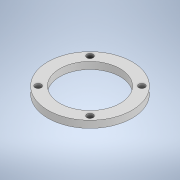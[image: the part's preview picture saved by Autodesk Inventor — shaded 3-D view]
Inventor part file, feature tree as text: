
AUTODESK INVENTOR PART (.ipt)
format: ipt  version: 2021 (Build 250183000, 183)  size: 117,760 bytes
history: native  units: mm
features: sketch x2, extrude x1, hole x1
ambient origin geometry x8: Origin, YZ Plane, XZ Plane, XY Plane, X Axis, Y Axis, Z Axis, Center Point
bodies: Solid1 (feature_tree)
feature tree (4):
  extrude  "Extrusion1"  Depth=60.0mm
  hole  "Hole1"  [1 undecoded]
  sketch  "Sketch1"  dims[d0=43.0mm d1=60.0mm]
  sketch  "Sketch2"  dims[d2=5.0mm d3=0.0mm d4=37.0mm d5=37.0mm d6=4.496mm d7=5.0mm d8=8.433mm d9=2.0mm d10=14.3117mm d11=6.0mm d12=0.0mm]
note: 1 required parameter value undecoded (feature->parameter linkage not recoverable at this tier; creation-order binding heuristic only, values carry confidence <= 0.55)
